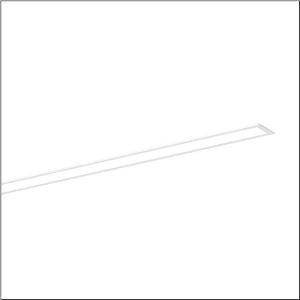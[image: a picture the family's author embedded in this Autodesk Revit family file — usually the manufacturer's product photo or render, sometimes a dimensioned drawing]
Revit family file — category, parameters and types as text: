
# Revit family: silica_r__21_51mx10tbt2w_f160
name_source: partatom
category: Lighting Fixtures
units: mm (PartAtom-declared; Revit-internal decimal feet)

## family parameters
Cut with Voids When Loaded = No
Host = Face
Light Source = No
Part Type = Normal
Room Calculation Point = No
Round Connector Dimension = Use Diameter
Shared = No

## types (1)
- --- (1 x LED, 3000 lm, 25.6 W, 6500K)
    Apparent Load = 26 VA
    CIE Flux Codes = 48 79 96 100 100
    Color Rendering = 80
    Color Temperature = 6500K
    Default Elevation = 1800 mm
    Description = Silica® 21, office luminaire, primary optical cover: cover, of PMMA, opal, light emission: direct distribution, primary light characteristic: symmetric, installation type: recessed, LED, rated luminous flux: 3.000lm, luminous efficacy: 112lm/W, light colour: 8tw, colour temperature: 2700..6500K, control gear: ECG DALI, with terminal, 3+2-pole, max. 2.5mm², mains connection: 220..240V, AC, 50/60Hz, rated input power: 26.9W, luminaire housing, of aluminium, traffic white (RAL 9016), length: 1.504mm, width: 77mm, height: 53mm, protection rating (complete): IP20, insulation class (complete): insulation class I (protective earthing), certification: CE, permissible operating ambient temperature: 0..+35°C, standard: EN 50419, packaging unit: 1 piece
    Height = 0 mm  [stored 0 ft]
    Lamp = 1 x LED
    Lamp Light Flux = 3000 lm
    Lamp Power = 25.6 W
    Lamp count = 1
    Length = 1527 mm
    Luminous efficacy = 117 lm/W
    Manufacturer = Siteco
    ModVariant = No
    Model = 51MX10TBT2W
    Mounting Place = Ceiling
    Mounting Type = Recessed
    Number of Poles = 1
    OnlyDefault = Yes
    Power Factor = 1
    Product Name = Silica® 21
    Product group = office luminaire | ceiling recessed
    ProductGroupID = 401
    Protection Class = Protection class I
    Protection Degree = IP 20
    RLX_Detail_Level = 1
    RLX_Emergency_Light_Flux = 0 lm
    RLX_Emergency_Type = 0
    RLX_Emergency_Type_DB = No
    RlxData = <blob elided: 17929 chars, md5=c5526017>
    Socket = socket
    Standby Power = 0 W
    System Light Flux = 3000 lm
    System Power = 26 W
    Type Comments = individual setting
    Type Image = l_1313615.jpg
    URL = http://relux.com
    VarID = @adj_089091
    Voltage = 0 V
    Weight = 0.00 kg
    Width = 79 mm

note: [stored X ft] marks values corroborated as IEEE doubles in the binary element streams (Revit-internal decimal feet)

## geometry (parser evidence)
native form markers: Blend x4, Sweep x11
no freeform markers — native parametric forms only
